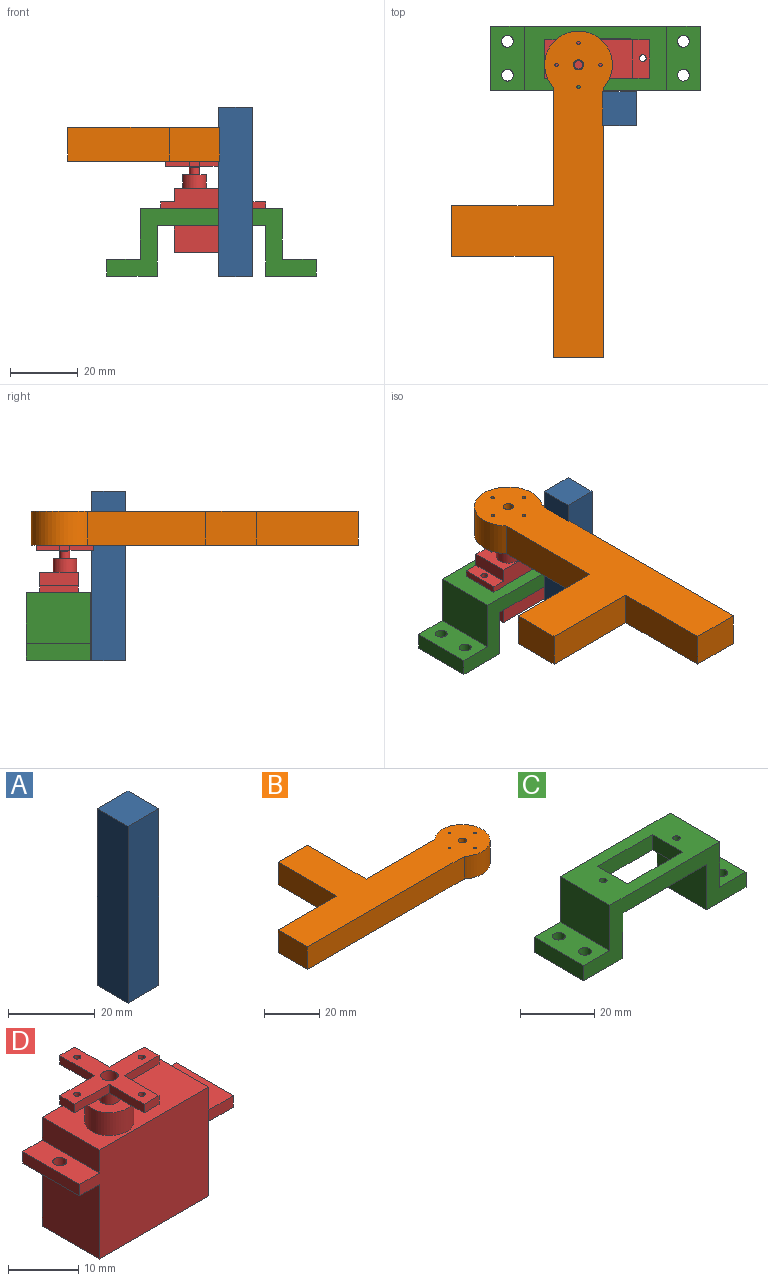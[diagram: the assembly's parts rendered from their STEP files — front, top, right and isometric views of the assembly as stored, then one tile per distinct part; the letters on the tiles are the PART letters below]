
ASSEMBLY  parts=4 mates=2
PART A: 8 faces, bbox 10x10x50 mm
  f0: plane 50x10mm, normal (1,0,0), area 500mm2, adj f1,f3,f4,f5
  f1: plane 50x10mm, normal (0,1,0), area 500mm2, adj f0,f2,f4,f5
  f2: plane 50x10mm, normal (-1,0,0), area 500mm2, adj f1,f3,f4,f5
  f3: plane 50x10mm, normal (0,-1,0), area 500mm2, adj f0,f2,f4,f5
  f4: plane 10x10mm, normal (0,0,1), area 100mm2, adj f0,f1,f2,f3
  f5: plane 10x10mm, normal (0,0,-1), area 92.9mm2, adj f0,f1,f2,f3,f6
  f6: cylinder r=1.5mm len=20mm, axis (0,0,-1), area 188.5mm2, adj f5,f7
  f7: plane 3x3mm, normal (0,0,-1), area 7.1mm2, adj f6
PART B: 15 faces, bbox 96.6x47.5x10 mm
  f0: cylinder r=10mm len=20mm, axis (0,0,-1), area 458.7mm2, adj f1,f12,f13,f14
  f1: plane 35x10mm, normal (0,1,0), area 350mm2, adj f0,f2,f13,f14
  f2: plane 30x10mm, normal (1,0,0), area 300mm2, adj f1,f3,f13,f14
  f3: plane 15x10mm, normal (0,1,0), area 150mm2, adj f2,f4,f13,f14
  f4: plane 30x10mm, normal (-1,0,0), area 300mm2, adj f3,f5,f13,f14
  f5: plane 30x10mm, normal (0,1,0), area 300mm2, adj f4,f6,f13,f14
  f6: plane 15x10mm, normal (-1,0,0), area 150mm2, adj f5,f12,f13,f14
  f7: cylinder r=1.5mm len=10mm, axis (0,0,-1), area 94.2mm2, adj f13,f14
  f8: cylinder r=0.5mm len=10mm, axis (0,0,-1), area 31.4mm2, adj f13,f14
  f9: cylinder r=0.5mm len=10mm, axis (0,0,-1), area 31.4mm2, adj f13,f14
  f10: cylinder r=0.5mm len=10mm, axis (0,0,-1), area 31.4mm2, adj f13,f14
  f11: cylinder r=0.5mm len=10mm, axis (0,0,-1), area 31.4mm2, adj f13,f14
  f12: plane 80x10mm, normal (0,-1,0), area 800mm2, adj f0,f6,f13,f14
  f13: plane 96.61x47.5mm, normal (0,0,1), area 1918.8mm2, adj f0,f1,f2,f3,f4,f5,f6,f7
  f14: plane 96.61x47.5mm, normal (0,0,-1), area 1918.8mm2, adj f0,f1,f2,f3,f4,f5,f6,f7
PART C: 24 faces, bbox 62x19x20 mm
  f0: plane 32x19mm, normal (0,0,-1), area 360.2mm2, adj f6,f7,f12,f13,f14,f15,f16,f17
  f1: plane 42x19mm, normal (0,0,1), area 550.2mm2, adj f2,f11,f12,f13,f14,f15,f16,f17
  f2: plane 19x15mm, normal (-1,0,0), area 285mm2, adj f1,f3,f12,f13
  f3: plane 19x10mm, normal (0,0,1), area 170.8mm2, adj f2,f4,f12,f13,f22,f23
  f4: plane 19x5mm, normal (-1,0,0), area 95mm2, adj f3,f5,f12,f13
  f5: plane 19x15mm, normal (0,0,-1), area 265.8mm2, adj f4,f6,f12,f13,f22,f23
  f6: plane 19x15mm, normal (1,0,0), area 285mm2, adj f0,f5,f12,f13
  f7: plane 19x15mm, normal (-1,0,0), area 285mm2, adj f0,f8,f12,f13
  f8: plane 19x15mm, normal (0,0,-1), area 265.8mm2, adj f7,f9,f12,f13,f20,f21
  f9: plane 19x5mm, normal (1,0,0), area 95mm2, adj f8,f10,f12,f13
  f10: plane 19x10mm, normal (0,0,1), area 170.8mm2, adj f9,f11,f12,f13,f20,f21
  f11: plane 19x15mm, normal (1,0,0), area 285mm2, adj f1,f10,f12,f13
  f12: plane 62x20mm, normal (0,-1,0), area 460mm2, adj f0,f1,f2,f3,f4,f5,f6,f7
  f13: plane 62x20mm, normal (0,1,0), area 460mm2, adj f0,f1,f2,f3,f4,f5,f6,f7
  f14: plane 11.5x5mm, normal (-1,0,0), area 57.5mm2, adj f0,f1,f15,f17
  f15: plane 21x5mm, normal (0,-1,0), area 105mm2, adj f0,f1,f14,f16
  f16: plane 11.5x5mm, normal (1,0,0), area 57.5mm2, adj f0,f1,f15,f17
  f17: plane 21x5mm, normal (0,1,0), area 105mm2, adj f0,f1,f14,f16
  f18: cylinder r=1mm len=5mm, axis (0,0,1), area 31.4mm2, adj f0,f1
  f19: cylinder r=1mm len=5mm, axis (0,0,1), area 31.4mm2, adj f0,f1
  f20: cylinder r=1.75mm len=5mm, axis (0,0,1), area 55mm2, adj f8,f10
  f21: cylinder r=1.75mm len=5mm, axis (0,0,1), area 55mm2, adj f8,f10
  f22: cylinder r=1.75mm len=5mm, axis (0,0,1), area 55mm2, adj f3,f5
  f23: cylinder r=1.75mm len=5mm, axis (0,0,1), area 55mm2, adj f3,f5
PART D: 41 faces, bbox 31x17x27 mm
  f0: plane 11.5x4mm, normal (-1,0,0), area 46mm2, adj f3,f5,f6,f16
  f1: plane 13x11.5mm, normal (1,0,0), area 149.5mm2, adj f3,f5,f7,f11
  f2: plane 13x11.5mm, normal (-1,0,0), area 149.5mm2, adj f3,f5,f7,f15
  f3: plane 26x19mm, normal (0,-1,0), area 426mm2, adj f0,f1,f2,f4,f6,f7,f10,f15
  f4: plane 11.5x4mm, normal (1,0,0), area 46mm2, adj f3,f5,f6,f13
  f5: plane 26x19mm, normal (0,1,0), area 426mm2, adj f0,f1,f2,f4,f6,f7,f12,f15
  f6: plane 22x11.5mm, normal (0,0,1), area 214.5mm2, adj f0,f3,f4,f5,f8
  f7: plane 22x11.5mm, normal (0,0,-1), area 253mm2, adj f1,f2,f3,f5
  f8: cylinder r=3.5mm len=7mm, axis (0,0,-1), area 88mm2, adj f6,f9
  f9: plane 7x7mm, normal (0,0,1), area 31.4mm2, adj f8,f18
  f10: plane 5x2mm, normal (0,-1,0), area 10mm2, adj f3,f11,f13,f14
  f11: plane 11.5x5mm, normal (0,0,-1), area 54.4mm2, adj f1,f10,f12,f14,f20
  f12: plane 5x2mm, normal (0,1,0), area 10mm2, adj f5,f11,f13,f14
  f13: plane 11.5x5mm, normal (0,0,1), area 54.4mm2, adj f4,f10,f12,f14,f20
  f14: plane 11.5x2mm, normal (1,0,0), area 23mm2, adj f10,f11,f12,f13
  f15: plane 11.5x4mm, normal (0,0,-1), area 42.9mm2, adj f2,f3,f5,f17,f19
  f16: plane 11.5x4mm, normal (0,0,1), area 42.9mm2, adj f0,f3,f5,f17,f19
  f17: plane 11.5x2mm, normal (-1,0,0), area 23mm2, adj f3,f5,f15,f16
  f18: cylinder r=1.5mm len=3mm, axis (0,0,-1), area 23.6mm2, adj f9,f34
  f19: cylinder r=1mm len=2mm, axis (0,0,1), area 12.6mm2, adj f15,f16
  f20: cylinder r=1mm len=2mm, axis (0,0,1), area 12.6mm2, adj f11,f13
  f21: plane 7x1.5mm, normal (0,1,0), area 10.5mm2, adj f22,f32,f33,f34
  f22: plane 3x1.5mm, normal (-1,0,0), area 4.5mm2, adj f21,f23,f33,f34
  f23: plane 7x1.5mm, normal (0,-1,0), area 10.5mm2, adj f22,f24,f33,f34
  f24: plane 7x1.5mm, normal (-1,0,0), area 10.5mm2, adj f23,f25,f33,f34
  f25: plane 3x1.5mm, normal (0,-1,0), area 4.5mm2, adj f24,f26,f33,f34
  f26: plane 7x1.5mm, normal (1,0,0), area 10.5mm2, adj f25,f27,f33,f34
  f27: plane 7x1.5mm, normal (0,-1,0), area 10.5mm2, adj f26,f28,f33,f34
  f28: plane 3x1.5mm, normal (1,0,0), area 4.5mm2, adj f27,f29,f33,f34
  f29: plane 7x1.5mm, normal (0,1,0), area 10.5mm2, adj f28,f30,f33,f34
  f30: plane 7x1.5mm, normal (1,0,0), area 10.5mm2, adj f29,f31,f33,f34
  f31: plane 3x1.5mm, normal (0,1,0), area 4.5mm2, adj f30,f32,f33,f34
  f32: plane 7x1.5mm, normal (-1,0,0), area 10.5mm2, adj f21,f31,f33,f34
  f33: plane 17x17mm, normal (0,0,1), area 84.9mm2, adj f21,f22,f23,f24,f25,f26,f27,f28
  f34: plane 17x17mm, normal (0,0,-1), area 82.8mm2, adj f18,f21,f22,f23,f24,f25,f26,f27
  f35: cylinder r=0.5mm len=1.5mm, axis (0,0,1), area 4.7mm2, adj f33,f34
  f36: cylinder r=0.5mm len=1.5mm, axis (0,0,1), area 4.7mm2, adj f33,f34
  f37: cylinder r=0.5mm len=1.5mm, axis (0,0,1), area 4.7mm2, adj f33,f34
  f38: cylinder r=0.5mm len=1.5mm, axis (0,0,1), area 4.7mm2, adj f33,f34
  f39: cylinder r=1.25mm len=2.5mm, axis (0,0,1), area 15.7mm2, adj f33,f40
  f40: plane 2.5x2.5mm, normal (0,0,1), area 4.9mm2, adj f39
PLACE A t=(7.11,-24.42,-17.61)mm
PLACE B rot(axis=(0,0,1),90deg) t=(-5,-11.5,16.5)mm
PLACE C at identity fixed
PLACE D t=(10.75,-5.7,-10.5)mm
MATE revolute B.f0 <-> D.f8  axis (0,0,-1) through (-5,-11.5,16.5)mm
MATE fastened D.f20 <-> C.f18  axis (0,0,-1) through (14,-9.5,2.5)mm
